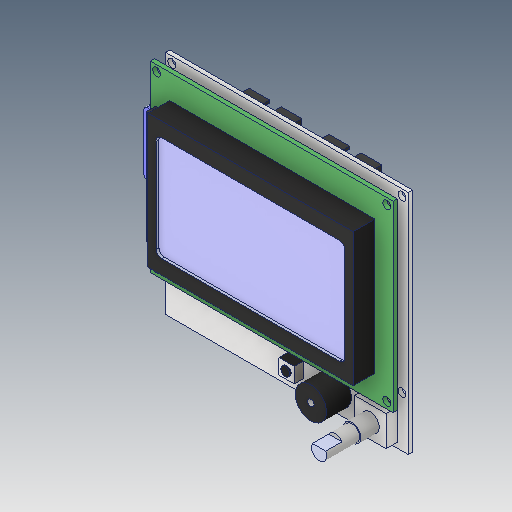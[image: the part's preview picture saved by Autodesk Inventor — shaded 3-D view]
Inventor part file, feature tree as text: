
AUTODESK INVENTOR PART (.ipt)
format: ipt  version: 2017 (Build 210142000, 142)  size: 209,920 bytes
history: native  units: mm
features: fillet x1
ambient origin geometry x8: Origin, YZ Plane, XZ Plane, XY Plane, X Axis, Y Axis, Z Axis, Center Point
bodies: Solid1 (feature_tree)
feature tree (1):
  fillet  "Fillet1 - SD Card"  [1 undecoded]
note: 1 required parameter value undecoded (feature->parameter linkage not recoverable at this tier; creation-order binding heuristic only, values carry confidence <= 0.55)
